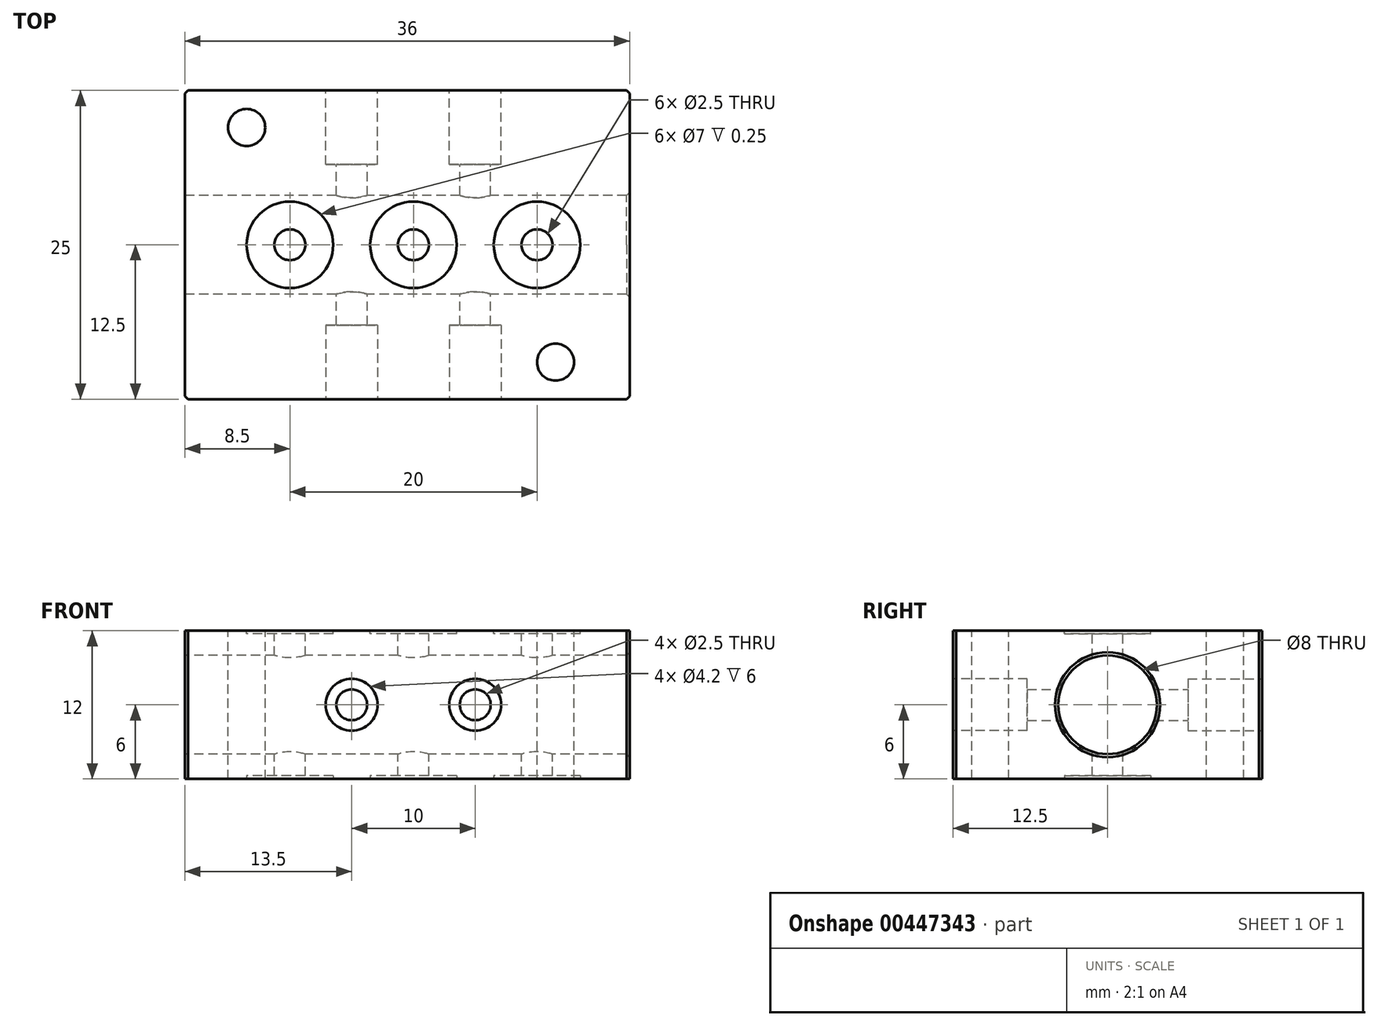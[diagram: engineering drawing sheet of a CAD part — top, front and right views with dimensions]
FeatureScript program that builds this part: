
annotation { "Feature Type Name" : "Feature", "Feature Type Description" : "" }
export const myFeature = defineFeature(function(context is Context, id is Id, definition is map)
    precondition{}
    {
        {
            var Q0;
            Q0=qCreatedBy(makeId("Top.planeOp"),FACE);
            var sketch = newSketch(context, id + "F0", { "sketchPlane" : qUnion([Q0])});
            skLineSegment(sketch, "E0.bottom", {"start": v(0, 0) * mm, "end": v(35, 0) * mm});
            skLineSegment(sketch, "E0.top", {"start": v(0, -25) * mm, "end": v(35, -25) * mm});
            skLineSegment(sketch, "E0.left", {"start": v(0, 0) * mm, "end": v(0, -25) * mm});
            skLineSegment(sketch, "E0.right", {"start": v(35, 0) * mm, "end": v(35, -25) * mm});
            skSolve(sketch);
        }
        {
            var Q0;
            Q0=makeQuery(id+"F0.imprint","IMPRINT",FACE,{"disambiguationData":[TD([[makeQuery(id+"F0.imprint","IMPRINT",EDGE,{"derivedFrom":sQuery(id+"F0.wireOp",EDGE,"E0.bottom")}),-1.0]])]});
            extrude(context, id + "F1", {"entities" : qUnion([Q0]), "depth" : 12 * mm, "offsetDistance" : 25 * mm});
        }
        {
            var Q0;
            Q0=makeQuery(id+"F1.opExtrude","SWEPT_FACE",FACE,{"disambiguationData":[OSD([sQuery(id+"F0.wireOp",EDGE,"E0.left")])]});
            var sketch = newSketch(context, id + "F2", { "sketchPlane" : qUnion([Q0])});
            skCircle(sketch, "E1", {"center": v(12.5, 6) * mm, "radius": 4 * mm});
            skPoint(sketch, "E1.centerSnap0", {"position": v(25, 6) * mm});
            skPoint(sketch, "E1.centerSnap1", {"position": v(12.5, 0) * mm});
            skLineSegment(sketch, "E2", {"start": v(12.5, 6) * mm, "end": v(25.77, 6) * mm, "construction": true});
            skSolve(sketch);
        }
        {
            var Q0;
            Q0=makeQuery(id+"F2.imprint","IMPRINT",FACE,{"disambiguationData":[TD([[makeQuery(id+"F2.imprint","IMPRINT",EDGE,{"derivedFrom":sQuery(id+"F2.wireOp",EDGE,"E1")}),1.0]])]});
            extrude(context, id + "F3", {"entities" : qUnion([Q0]), "operationType" : NewBodyOperationType.REMOVE, "endBound" : BoundingType.UP_TO_NEXT, "oppositeDirection" : true, "depth" : 25 * mm});
        }
        {
            var Q0;
            Q0=makeQuery(id+"F1.opExtrude","CAP_FACE",FACE,{"disambiguationData":[OSD([sQuery(id+"F0.wireOp",EDGE,"E0.bottom"),sQuery(id+"F0.wireOp",EDGE,"E0.top"),sQuery(id+"F0.wireOp",EDGE,"E0.left"),sQuery(id+"F0.wireOp",EDGE,"E0.right")])],"isStart":false});
            var sketch = newSketch(context, id + "F4", { "sketchPlane" : qUnion([Q0])});
            skLineSegment(sketch, "E3", {"start": v(28.5, -25) * mm, "end": v(28.5, 0) * mm, "construction": true});
            skLineSegment(sketch, "E4", {"start": v(18.5, -25) * mm, "end": v(18.5, 0) * mm, "construction": true});
            skCircle(sketch, "E5", {"center": v(28.5, -12.5) * mm, "radius": 1.25 * mm});
            skCircle(sketch, "E6", {"center": v(18.5, -12.5) * mm, "radius": 1.25 * mm});
            skLineSegment(sketch, "E7", {"start": v(35, -22) * mm, "end": v(30, -22) * mm, "construction": true});
            skLineSegment(sketch, "E8", {"start": v(30, -25) * mm, "end": v(30, -22) * mm, "construction": true});
            skLineSegment(sketch, "E9", {"start": v(0, -3) * mm, "end": v(5, -3) * mm, "construction": true});
            skLineSegment(sketch, "E10", {"start": v(5, -3) * mm, "end": v(5, 0) * mm, "construction": true});
            skCircle(sketch, "E11", {"center": v(30, -22) * mm, "radius": 1.5 * mm});
            skCircle(sketch, "E12", {"center": v(5, -3) * mm, "radius": 1.5 * mm});
            skLineSegment(sketch, "E13", {"start": v(8.5, -25) * mm, "end": v(8.5, 0) * mm, "construction": true});
            skCircle(sketch, "E14", {"center": v(8.5, -12.5) * mm, "radius": 1.25 * mm});
            skCircle(sketch, "E15", {"center": v(8.5, -12.5) * mm, "radius": 3.5 * mm});
            skCircle(sketch, "E16", {"center": v(18.5, -12.5) * mm, "radius": 3.5 * mm});
            skCircle(sketch, "E17", {"center": v(28.5, -12.5) * mm, "radius": 3.5 * mm});
            skSolve(sketch);
        }
        {
            var Q0;
            Q0=makeQuery(id+"F4.imprint","IMPRINT",FACE,{"disambiguationData":[TD([[makeQuery(id+"F4.imprint","IMPRINT",EDGE,{"derivedFrom":sQuery(id+"F4.wireOp",EDGE,"E14")}),-1.0]])]});
            var Q1;
            Q1=makeQuery(id+"F4.imprint","IMPRINT",FACE,{"disambiguationData":[TD([[makeQuery(id+"F4.imprint","IMPRINT",EDGE,{"derivedFrom":sQuery(id+"F4.wireOp",EDGE,"E6")}),-1.0]])]});
            var Q2;
            Q2=makeQuery(id+"F4.imprint","IMPRINT",FACE,{"disambiguationData":[TD([[makeQuery(id+"F4.imprint","IMPRINT",EDGE,{"derivedFrom":sQuery(id+"F4.wireOp",EDGE,"E5")}),-1.0]])]});
            extrude(context, id + "F5", {"entities" : qUnion([Q0, Q1, Q2]), "oppositeDirection" : true, "depth" : .25 * mm, "offsetDistance" : 25 * mm});
        }
        {
            var Q0;
            Q0=makeQuery(id+"F4.imprint","IMPRINT",FACE,{"disambiguationData":[TD([[makeQuery(id+"F4.imprint","IMPRINT",EDGE,{"derivedFrom":sQuery(id+"F4.wireOp",EDGE,"E11")}),1.0]])]});
            var Q1;
            Q1=makeQuery(id+"F4.imprint","IMPRINT",FACE,{"disambiguationData":[TD([[makeQuery(id+"F4.imprint","IMPRINT",EDGE,{"derivedFrom":sQuery(id+"F4.wireOp",EDGE,"E5")}),1.0]])]});
            var Q2;
            Q2=makeQuery(id+"F4.imprint","IMPRINT",FACE,{"disambiguationData":[TD([[makeQuery(id+"F4.imprint","IMPRINT",EDGE,{"derivedFrom":sQuery(id+"F4.wireOp",EDGE,"E6")}),1.0]])]});
            var Q3;
            Q3=makeQuery(id+"F4.imprint","IMPRINT",FACE,{"disambiguationData":[TD([[makeQuery(id+"F4.imprint","IMPRINT",EDGE,{"derivedFrom":sQuery(id+"F4.wireOp",EDGE,"E12")}),1.0]])]});
            var Q4;
            Q4=makeQuery(id+"F4.imprint","IMPRINT",FACE,{"disambiguationData":[TD([[makeQuery(id+"F4.imprint","IMPRINT",EDGE,{"derivedFrom":sQuery(id+"F4.wireOp",EDGE,"E14")}),1.0]])]});
            extrude(context, id + "F6", {"entities" : qUnion([Q0, Q1, Q2, Q3, Q4]), "operationType" : NewBodyOperationType.REMOVE, "oppositeDirection" : true, "depth" : 25 * mm});
        }
        {
            var Q0;
            Q0=makeQuery(id+"F1.opExtrude","SWEPT_FACE",FACE,{"disambiguationData":[OSD([sQuery(id+"F0.wireOp",EDGE,"E0.bottom")])]});
            var sketch = newSketch(context, id + "F7", { "sketchPlane" : qUnion([Q0])});
            skLineSegment(sketch, "E18", {"start": v(-23.5, 12) * mm, "end": v(-23.5, 0) * mm, "construction": true});
            skLineSegment(sketch, "E19", {"start": v(-13.5, 12) * mm, "end": v(-13.5, 0) * mm, "construction": true});
            skCircle(sketch, "E20", {"center": v(-23.5, 6) * mm, "radius": 1.25 * mm});
            skCircle(sketch, "E21", {"center": v(-13.5, 6) * mm, "radius": 1.25 * mm});
            skSolve(sketch);
        }
        {
            var Q0;
            Q0=makeQuery(id+"F7.imprint","IMPRINT",FACE,{"disambiguationData":[TD([[makeQuery(id+"F7.imprint","IMPRINT",EDGE,{"derivedFrom":sQuery(id+"F7.wireOp",EDGE,"E20")}),1.0]])]});
            var Q1;
            Q1=makeQuery(id+"F7.imprint","IMPRINT",FACE,{"disambiguationData":[TD([[makeQuery(id+"F7.imprint","IMPRINT",EDGE,{"derivedFrom":sQuery(id+"F7.wireOp",EDGE,"E21")}),1.0]])]});
            extrude(context, id + "F8", {"entities" : qUnion([Q0, Q1]), "operationType" : NewBodyOperationType.REMOVE, "oppositeDirection" : true, "depth" : 25 * mm});
        }
        {
            var Q0;
            Q0=makeQuery(id+"F1.opExtrude","SWEPT_FACE",FACE,{"disambiguationData":[OSD([sQuery(id+"F0.wireOp",EDGE,"E0.top")])]});
            var sketch = newSketch(context, id + "F9", { "sketchPlane" : qUnion([Q0])});
            skCircle(sketch, "E22", {"center": v(13.5, 6) * mm, "radius": 2.1 * mm});
            skCircle(sketch, "E23", {"center": v(23.5, 6) * mm, "radius": 2.1 * mm});
            skSolve(sketch);
        }
        {
            var Q0;
            Q0=makeQuery(id+"F1.opExtrude","SWEPT_FACE",FACE,{"disambiguationData":[OSD([sQuery(id+"F0.wireOp",EDGE,"E0.bottom")])]});
            var sketch = newSketch(context, id + "F10", { "sketchPlane" : qUnion([Q0])});
            skCircle(sketch, "E24", {"center": v(-13.5, 6) * mm, "radius": 2.1 * mm});
            skCircle(sketch, "E25", {"center": v(-23.5, 6) * mm, "radius": 2.1 * mm});
            skSolve(sketch);
        }
        {
            var Q0;
            Q0=makeQuery(id+"F10.imprint","IMPRINT",FACE,{"disambiguationData":[TD([[makeQuery(id+"F10.imprint","IMPRINT",EDGE,{"derivedFrom":sQuery(id+"F10.wireOp",EDGE,"E24")}),1.0]])]});
            var Q1;
            Q1=makeQuery(id+"F10.imprint","IMPRINT",FACE,{"disambiguationData":[TD([[makeQuery(id+"F10.imprint","IMPRINT",EDGE,{"derivedFrom":sQuery(id+"F10.wireOp",EDGE,"E25")}),1.0]])]});
            extrude(context, id + "F11", {"entities" : qUnion([Q0, Q1]), "operationType" : NewBodyOperationType.REMOVE, "oppositeDirection" : true, "depth" : 6 * mm, "offsetDistance" : 25 * mm});
        }
        {
            var Q0;
            Q0=makeQuery(id+"F9.imprint","IMPRINT",FACE,{"disambiguationData":[TD([[makeQuery(id+"F9.imprint","IMPRINT",EDGE,{"derivedFrom":sQuery(id+"F9.wireOp",EDGE,"E22")}),1.0]])]});
            var Q1;
            Q1=makeQuery(id+"F9.imprint","IMPRINT",FACE,{"disambiguationData":[TD([[makeQuery(id+"F9.imprint","IMPRINT",EDGE,{"derivedFrom":sQuery(id+"F9.wireOp",EDGE,"E23")}),1.0]])]});
            extrude(context, id + "F12", {"entities" : qUnion([Q0, Q1]), "operationType" : NewBodyOperationType.REMOVE, "oppositeDirection" : true, "depth" : 6 * mm, "offsetDistance" : 25 * mm});
        }
        {
            var Q0;
            Q0=makeQuery(id+"F1.opExtrude","SWEPT_FACE",FACE,{"disambiguationData":[OSD([sQuery(id+"F0.wireOp",EDGE,"E0.right")])]});
            extrude(context, id + "F13", {"entities" : qUnion([Q0]), "operationType" : NewBodyOperationType.ADD, "depth" : 1 * mm});
        }
        {
            var Q0;
            Q0=makeQuery(id+"F12.boolean.opBoolean","COPY",EDGE,{"derivedFrom":makeQuery(id+"F12.opExtrude","CAP_EDGE",EDGE,{"disambiguationData":[OSD([sQuery(id+"F9.wireOp",EDGE,"E22")])],"isStart":true})});
            var Q1;
            Q1=makeQuery(id+"F12.boolean.opBoolean","COPY",EDGE,{"derivedFrom":makeQuery(id+"F12.opExtrude","CAP_EDGE",EDGE,{"disambiguationData":[OSD([sQuery(id+"F9.wireOp",EDGE,"E23")])],"isStart":true})});
            var Q2;
            Q2=makeQuery(id+"F11.boolean.opBoolean","COPY",EDGE,{"derivedFrom":makeQuery(id+"F11.opExtrude","CAP_EDGE",EDGE,{"disambiguationData":[OSD([sQuery(id+"F10.wireOp",EDGE,"E24")])],"isStart":true})});
            var Q3;
            Q3=makeQuery(id+"F11.boolean.opBoolean","COPY",EDGE,{"derivedFrom":makeQuery(id+"F11.opExtrude","CAP_EDGE",EDGE,{"disambiguationData":[OSD([sQuery(id+"F10.wireOp",EDGE,"E25")])],"isStart":true})});
            var Q4;
            Q4=makeQuery(id+"F13.opExtrude","CAP_EDGE",EDGE,{"disambiguationData":[OSD([sQuery(id+"F0.wireOp",EDGE,"E0.right"),sQuery(id+"F2.wireOp",EDGE,"E1")])],"isStart":false});
            var Q5;
            Q5=makeQuery(id+"F3.boolean.opBoolean","COPY",EDGE,{"derivedFrom":makeQuery(id+"F3.opExtrude","CAP_EDGE",EDGE,{"disambiguationData":[OSD([sQuery(id+"F2.wireOp",EDGE,"E1")])],"isStart":true})});
            chamfer(context, id + "F14", {"entities" : qUnion([Q0, Q1, Q2, Q3, Q4, Q5]), "width" : .25 * mm, "tangentPropagation" : true});
        }
        {
            var Q0;
            Q0=makeQuery(id+"F13.opExtrude","CAP_EDGE",EDGE,{"disambiguationData":[OSD([sQuery(id+"F0.wireOp",EDGE,"E0.top"),sQuery(id+"F0.wireOp",EDGE,"E0.right")])],"isStart":false});
            var Q1;
            Q1=makeQuery(id+"F13.opExtrude","CAP_EDGE",EDGE,{"disambiguationData":[OSD([sQuery(id+"F0.wireOp",EDGE,"E0.bottom"),sQuery(id+"F0.wireOp",EDGE,"E0.right")])],"isStart":false});
            var Q2;
            Q2=makeQuery(id+"F1.opExtrude","SWEPT_EDGE",EDGE,{"disambiguationData":[OSD([sQuery(id+"F0.wireOp",EDGE,"E0.bottom"),sQuery(id+"F0.wireOp",EDGE,"E0.left")])]});
            var Q3;
            Q3=makeQuery(id+"F1.opExtrude","SWEPT_EDGE",EDGE,{"disambiguationData":[OSD([sQuery(id+"F0.wireOp",EDGE,"E0.top"),sQuery(id+"F0.wireOp",EDGE,"E0.left")])]});
            chamfer(context, id + "F15", {"entities" : qUnion([Q0, Q1, Q2, Q3]), "width" : .25 * mm, "tangentPropagation" : true});
        }
        {
            var Q0;
            Q0=makeQuery(id+"F5.opExtrude","SWEPT_BODY",BODY,{"disambiguationData":[OSD([sQuery(id+"F4.wireOp",EDGE,"d52e03b5-0367-475b-933c-931b53422793"),sQuery(id+"F4.wireOp",EDGE,"E15")])]});
            var Q1;
            Q1=makeQuery(id+"F5.opExtrude","SWEPT_BODY",BODY,{"disambiguationData":[OSD([sQuery(id+"F4.wireOp",EDGE,"e90380dc-318a-4735-891d-ac750ae70b11"),sQuery(id+"F4.wireOp",EDGE,"E16")])]});
            var Q2;
            Q2=makeQuery(id+"F5.opExtrude","SWEPT_BODY",BODY,{"disambiguationData":[OSD([sQuery(id+"F4.wireOp",EDGE,"224a60a9-792f-4f5f-8ca1-9c68640039a2"),sQuery(id+"F4.wireOp",EDGE,"E17")])]});
            var Q3;
            Q3=qCreatedBy(makeId("Top.planeOp"),FACE);
            mirror(context, id + "F16", {"entities" : qUnion([Q0, Q1, Q2]), "mirrorPlane" : qUnion([Q3])});
        }
        {
            var Q0;
            Q0=makeQuery(id+"F16.opPattern","COPY",BODY,{"derivedFrom":makeQuery(id+"F5.opExtrude","SWEPT_BODY",BODY,{"disambiguationData":[OSD([sQuery(id+"F4.wireOp",EDGE,"224a60a9-792f-4f5f-8ca1-9c68640039a2"),sQuery(id+"F4.wireOp",EDGE,"E17")])]}),"instanceName":"1"});
            var Q1;
            Q1=makeQuery(id+"F16.opPattern","COPY",BODY,{"derivedFrom":makeQuery(id+"F5.opExtrude","SWEPT_BODY",BODY,{"disambiguationData":[OSD([sQuery(id+"F4.wireOp",EDGE,"e90380dc-318a-4735-891d-ac750ae70b11"),sQuery(id+"F4.wireOp",EDGE,"E16")])]}),"instanceName":"1"});
            var Q2;
            Q2=makeQuery(id+"F16.opPattern","COPY",BODY,{"derivedFrom":makeQuery(id+"F5.opExtrude","SWEPT_BODY",BODY,{"disambiguationData":[OSD([sQuery(id+"F4.wireOp",EDGE,"d52e03b5-0367-475b-933c-931b53422793"),sQuery(id+"F4.wireOp",EDGE,"E15")])]}),"instanceName":"1"});
            var Q3;
            {var subQ0=sQuery(id+"F0.wireOp",EDGE,"E0.top");Q3=makeQuery(id+"F15.opChamfer","BLEND_EDGE",EDGE,{"blendedFrom":[makeQuery(id+"F1.opExtrude","SWEPT_EDGE",EDGE,{"disambiguationData":[OSD([subQ0,sQuery(id+"F0.wireOp",EDGE,"E0.left")])]}),makeQuery(id+"F13.boolean.opBoolean","MERGE",FACE,{"derivedFrom":[makeQuery(id+"F1.opExtrude","SWEPT_FACE",FACE,{"disambiguationData":[OSD([subQ0])]}),makeQuery(id+"F13.opExtrude","SWEPT_FACE",FACE,{"disambiguationData":[OSD([subQ0,sQuery(id+"F0.wireOp",EDGE,"E0.right")])]})]})],"blendedInto":[makeQuery(id+"F13.boolean.opBoolean","MERGE",FACE,{"derivedFrom":[makeQuery(id+"F1.opExtrude","SWEPT_FACE",FACE,{"disambiguationData":[OSD([subQ0])]}),makeQuery(id+"F13.opExtrude","SWEPT_FACE",FACE,{"disambiguationData":[OSD([subQ0,sQuery(id+"F0.wireOp",EDGE,"E0.right")])]})]})]});}
            transform(context, id + "F17", {"entities" : qUnion([Q0, Q1, Q2]), "transformType" : TransformType.TRANSLATION_DISTANCE, "transformDirection" : qUnion([Q3]), "distance" : 12 * mm, "oppositeDirection" : true, "makeCopy" : false});
        }
        {
            var Q0;
            Q0=makeQuery(id+"F5.opExtrude","SWEPT_BODY",BODY,{"disambiguationData":[OSD([sQuery(id+"F4.wireOp",EDGE,"224a60a9-792f-4f5f-8ca1-9c68640039a2"),sQuery(id+"F4.wireOp",EDGE,"E17")])]});
            var Q1;
            Q1=makeQuery(id+"F5.opExtrude","SWEPT_BODY",BODY,{"disambiguationData":[OSD([sQuery(id+"F4.wireOp",EDGE,"d52e03b5-0367-475b-933c-931b53422793"),sQuery(id+"F4.wireOp",EDGE,"E15")])]});
            var Q2;
            Q2=makeQuery(id+"F5.opExtrude","SWEPT_BODY",BODY,{"disambiguationData":[OSD([sQuery(id+"F4.wireOp",EDGE,"e90380dc-318a-4735-891d-ac750ae70b11"),sQuery(id+"F4.wireOp",EDGE,"E16")])]});
            var Q3;
            Q3=makeQuery(id+"F16.opPattern","COPY",BODY,{"derivedFrom":makeQuery(id+"F5.opExtrude","SWEPT_BODY",BODY,{"disambiguationData":[OSD([sQuery(id+"F4.wireOp",EDGE,"d52e03b5-0367-475b-933c-931b53422793"),sQuery(id+"F4.wireOp",EDGE,"E15")])]}),"instanceName":"1"});
            var Q4;
            Q4=makeQuery(id+"F16.opPattern","COPY",BODY,{"derivedFrom":makeQuery(id+"F5.opExtrude","SWEPT_BODY",BODY,{"disambiguationData":[OSD([sQuery(id+"F4.wireOp",EDGE,"e90380dc-318a-4735-891d-ac750ae70b11"),sQuery(id+"F4.wireOp",EDGE,"E16")])]}),"instanceName":"1"});
            var Q5;
            Q5=makeQuery(id+"F16.opPattern","COPY",BODY,{"derivedFrom":makeQuery(id+"F5.opExtrude","SWEPT_BODY",BODY,{"disambiguationData":[OSD([sQuery(id+"F4.wireOp",EDGE,"224a60a9-792f-4f5f-8ca1-9c68640039a2"),sQuery(id+"F4.wireOp",EDGE,"E17")])]}),"instanceName":"1"});
            var Q6;
            Q6=makeQuery(id+"F1.opExtrude","SWEPT_BODY",BODY,{"disambiguationData":[OSD([sQuery(id+"F0.wireOp",EDGE,"E0.bottom"),sQuery(id+"F0.wireOp",EDGE,"E0.top"),sQuery(id+"F0.wireOp",EDGE,"E0.left"),sQuery(id+"F0.wireOp",EDGE,"E0.right")])]});
            booleanBodies(context, id + "F18", {"operationType" : BooleanOperationType.SUBTRACTION, "tools" : qUnion([Q0, Q1, Q2, Q3, Q4, Q5]), "targets" : qUnion([Q6])});
        }
    });
